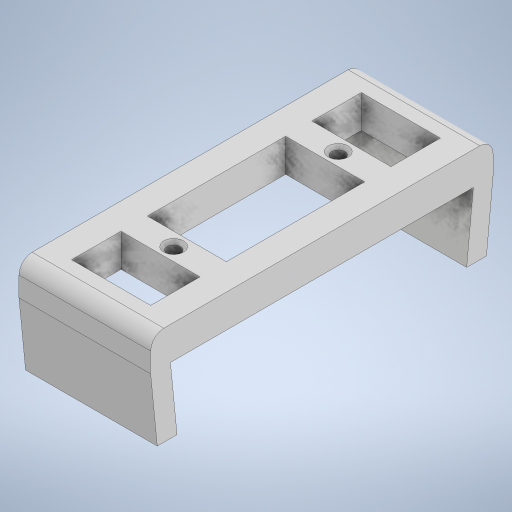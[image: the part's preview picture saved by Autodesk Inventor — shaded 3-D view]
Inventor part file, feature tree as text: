
AUTODESK INVENTOR PART (.ipt)
format: ipt  version: 2023 (Build 270158000, 158)  size: 279,552 bytes
history: native  units: mm
features: sketch x3, extrude x2, other x1, hole x1, fillet x1
ambient origin geometry x8: Origin, YZ Plane, XZ Plane, XY Plane, X Axis, Y Axis, Z Axis, Center Point
bodies: Body1 (feature_tree)
feature tree (8):
  other  "솔리드1"
  extrude  "돌출1"  Depth=20.0mm
  hole  "구멍1"  [1 undecoded]
  extrude  "돌출2"  Depth=4.0mm
  fillet  "모깎기1"  Radius=15.5mm
  sketch  "스케치1"
  sketch  "스케치2"
  sketch  "스케치3"
note: 1 required parameter value undecoded (feature->parameter linkage not recoverable at this tier; creation-order binding heuristic only, values carry confidence <= 0.55)
